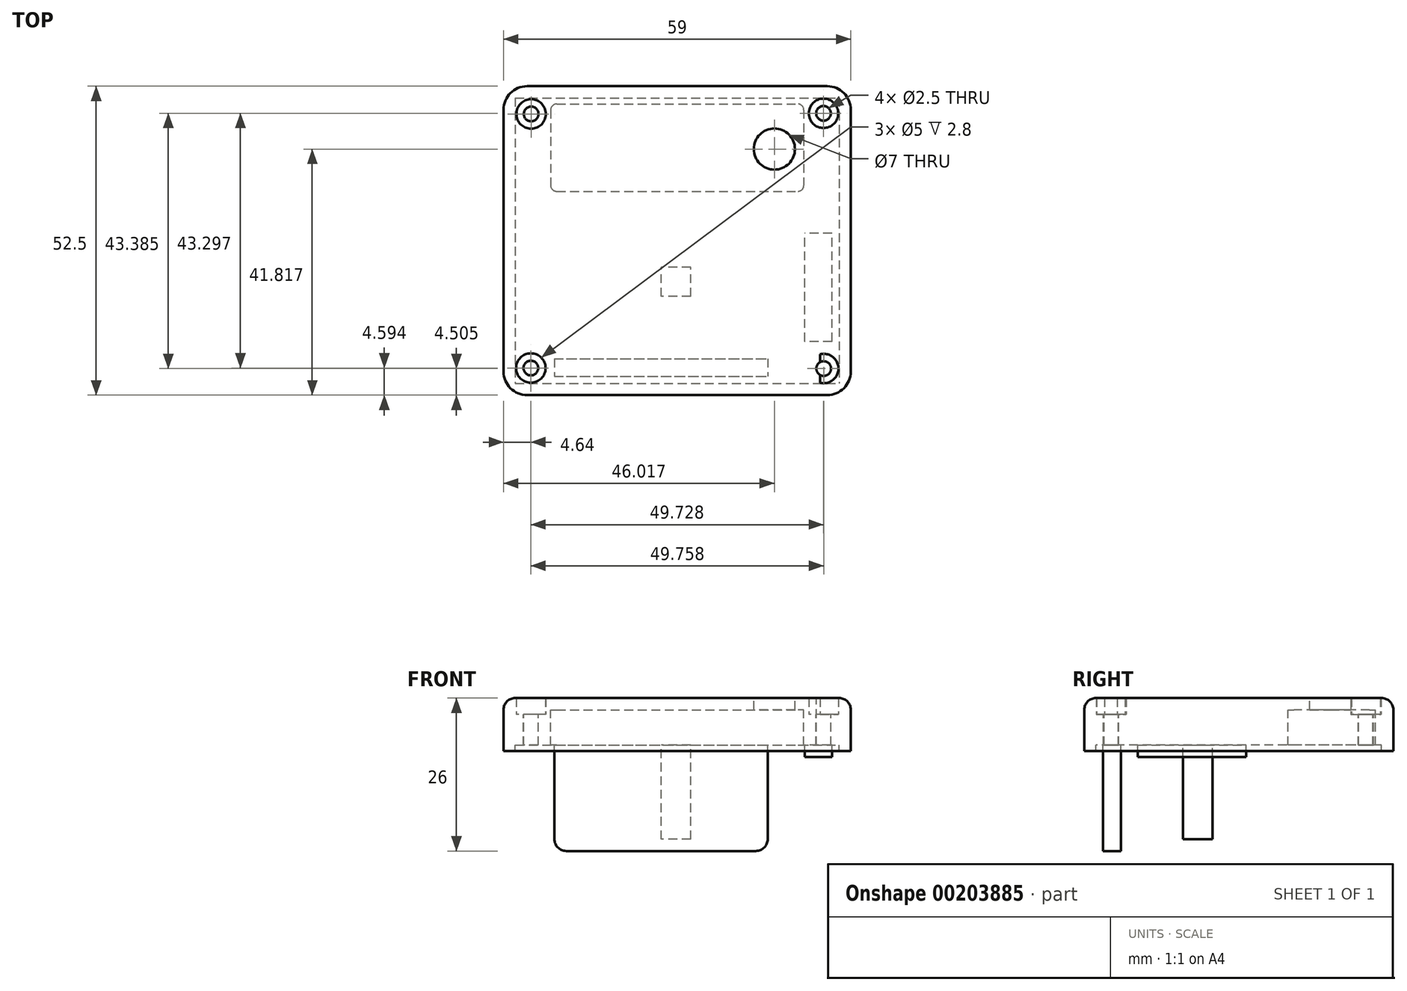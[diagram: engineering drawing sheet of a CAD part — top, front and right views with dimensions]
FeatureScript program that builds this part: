
annotation { "Feature Type Name" : "Feature", "Feature Type Description" : "" }
export const myFeature = defineFeature(function(context is Context, id is Id, definition is map)
    precondition{}
    {
        {
            var Q0;
            Q0=qCreatedBy(makeId("Top.planeOp"),FACE);
            var sketch = newSketch(context, id + "F0", { "sketchPlane" : qUnion([Q0])});
            skLineSegment(sketch, "E0.bottom", {"start": v(-36.58, 35.75) * mm, "end": v(22.42, 35.75) * mm});
            skLineSegment(sketch, "E0.top", {"start": v(-36.58, -16.75) * mm, "end": v(22.42, -16.75) * mm});
            skLineSegment(sketch, "E0.left", {"start": v(-36.58, 35.75) * mm, "end": v(-36.58, -16.75) * mm});
            skLineSegment(sketch, "E0.right", {"start": v(22.42, 35.75) * mm, "end": v(22.42, -16.75) * mm});
            skLineSegment(sketch, "E1.bottom", {"start": v(-34.58, 33.75) * mm, "end": v(20.42, 33.75) * mm});
            skLineSegment(sketch, "E1.top", {"start": v(-34.58, -14.75) * mm, "end": v(20.42, -14.75) * mm});
            skLineSegment(sketch, "E1.left", {"start": v(-34.58, 33.75) * mm, "end": v(-34.58, -14.75) * mm});
            skLineSegment(sketch, "E1.right", {"start": v(20.42, 33.75) * mm, "end": v(20.42, -14.75) * mm});
            skLineSegment(sketch, "E2.right", {"start": v(-34.58, -2) * mm, "end": v(-34.58, 2) * mm});
            skLineSegment(sketch, "E3.bottom", {"start": v(-34.58, 33.75) * mm, "end": v(9.72, 33.75) * mm});
            skLineSegment(sketch, "E4.top", {"start": v(-34.58, -14.75) * mm, "end": v(-32.58, -14.75) * mm});
            skLineSegment(sketch, "E4.left", {"start": v(-34.58, -8.75) * mm, "end": v(-34.58, -14.75) * mm});
            skLineSegment(sketch, "E5.bottom", {"start": v(13.36, 33.75) * mm, "end": v(14.86, 33.75) * mm});
            skLineSegment(sketch, "E6.top", {"start": v(16.3, -14.75) * mm, "end": v(14.92, -14.75) * mm});
            skLineSegment(sketch, "E7.bottom", {"start": v(17.21, 9.77) * mm, "end": v(11.21, 9.77) * mm});
            skLineSegment(sketch, "E7.top", {"start": v(17.21, 4.77) * mm, "end": v(11.21, 4.77) * mm});
            skLineSegment(sketch, "E7.left", {"start": v(17.21, 9.77) * mm, "end": v(17.21, 4.77) * mm});
            skLineSegment(sketch, "E7.right", {"start": v(11.21, 9.77) * mm, "end": v(11.21, 4.77) * mm});
            skCircle(sketch, "E8", {"center": v(-31.94, -12.16) * mm, "radius": 1.25 * mm});
            skCircle(sketch, "E9", {"center": v(-31.9, 31.03) * mm, "radius": 2.5 * mm});
            skCircle(sketch, "E10", {"center": v(-31.9, 31.03) * mm, "radius": 1.25 * mm});
            skLineSegment(sketch, "E11", {"start": v(-29.4, 31.03) * mm, "end": v(-29.4, 33.75) * mm});
            skLineSegment(sketch, "E12", {"start": v(-31.9, 28.53) * mm, "end": v(-34.58, 28.53) * mm});
            skLineSegment(sketch, "E13.bottom", {"start": v(17.22, 16.75) * mm, "end": v(-34.58, 16.75) * mm});
            skLineSegment(sketch, "E13.top", {"start": v(17.22, 15.25) * mm, "end": v(-34.58, 15.25) * mm});
            skLineSegment(sketch, "E13.left", {"start": v(17.22, 15.25) * mm, "end": v(17.22, 16.75) * mm});
            skLineSegment(sketch, "E13.right", {"start": v(-34.58, 15.25) * mm, "end": v(-34.58, 16.75) * mm});
            skLineSegment(sketch, "E14.bottom", {"start": v(-34.58, 14.63) * mm, "end": v(-32.58, 14.63) * mm});
            skLineSegment(sketch, "E14.top", {"start": v(-34.58, 8.63) * mm, "end": v(-32.58, 8.63) * mm});
            skLineSegment(sketch, "E14.left", {"start": v(-34.58, 14.63) * mm, "end": v(-34.58, 8.63) * mm});
            skLineSegment(sketch, "E14.right", {"start": v(-32.58, 14.63) * mm, "end": v(-32.58, 8.63) * mm});
            skCircle(sketch, "E15", {"center": v(17.79, 31.14) * mm, "radius": 2.5 * mm});
            skCircle(sketch, "E16", {"center": v(17.79, 31.14) * mm, "radius": 1.25 * mm});
            skLineSegment(sketch, "E17", {"start": v(17.79, 28.64) * mm, "end": v(20.42, 28.64) * mm});
            skCircle(sketch, "E18", {"center": v(17.82, -12.24) * mm, "radius": 2.5 * mm});
            skCircle(sketch, "E19", {"center": v(17.82, -12.24) * mm, "radius": 1.25 * mm});
            skLineSegment(sketch, "E20", {"start": v(17.82, -9.74) * mm, "end": v(20.42, -9.74) * mm});
            skLineSegment(sketch, "E21.bottom", {"start": v(14.92, -14.75) * mm, "end": v(13.15, -14.75) * mm});
            skLineSegment(sketch, "E21.top", {"start": v(14.92, -13.29) * mm, "end": v(13.15, -13.29) * mm});
            skLineSegment(sketch, "E21.left", {"start": v(14.92, -14.75) * mm, "end": v(14.92, -13.29) * mm});
            skLineSegment(sketch, "E21.right", {"start": v(13.15, -14.75) * mm, "end": v(13.15, -13.29) * mm});
            skLineSegment(sketch, "E22", {"start": v(17.22, 33.75) * mm, "end": v(17.22, -14.75) * mm});
            skLineSegment(sketch, "E23", {"start": v(20.42, -9.02) * mm, "end": v(17.22, -9.02) * mm});
            skLineSegment(sketch, "E24.top", {"start": v(14.92, -7.79) * mm, "end": v(13.15, -7.79) * mm});
            skLineSegment(sketch, "E24.left", {"start": v(14.92, -13.29) * mm, "end": v(14.92, -7.79) * mm});
            skLineSegment(sketch, "E24.right", {"start": v(13.15, -13.29) * mm, "end": v(13.15, -7.79) * mm});
            skLineSegment(sketch, "E25", {"start": v(15.29, 31.14) * mm, "end": v(15.29, 33.75) * mm});
            skLineSegment(sketch, "E26", {"start": v(15.32, -12.24) * mm, "end": v(15.32, -14.75) * mm});
            skLineSegment(sketch, "E27.bottom", {"start": v(-29.94, 15.25) * mm, "end": v(10.06, 15.25) * mm});
            skLineSegment(sketch, "E27.top", {"start": v(-29.94, 13.25) * mm, "end": v(10.06, 13.25) * mm});
            skLineSegment(sketch, "E27.left", {"start": v(-29.94, 15.25) * mm, "end": v(-29.94, 13.25) * mm});
            skLineSegment(sketch, "E27.right", {"start": v(10.06, 15.25) * mm, "end": v(10.06, 13.25) * mm});
            skLineSegment(sketch, "E28.bottom", {"start": v(-19.58, -1.75) * mm, "end": v(5.42, -1.75) * mm});
            skLineSegment(sketch, "E28.top", {"start": v(-19.58, 7.25) * mm, "end": v(5.42, 7.25) * mm});
            skLineSegment(sketch, "E28.left", {"start": v(-19.58, -1.75) * mm, "end": v(-19.58, 7.25) * mm});
            skLineSegment(sketch, "E28.right", {"start": v(5.42, -1.75) * mm, "end": v(5.42, 7.25) * mm});
            skCircle(sketch, "E29", {"center": v(9.44, 25.07) * mm, "radius": 3.5 * mm});
            skLineSegment(sketch, "E30", {"start": v(-29.58, 15.25) * mm, "end": v(-29.58, -14.75) * mm, "construction": true});
            skLineSegment(sketch, "E31", {"start": v(17.22, 1.25) * mm, "end": v(-34.58, 1.25) * mm, "construction": true});
            skLineSegment(sketch, "E32", {"start": v(-34.58, 6.25) * mm, "end": v(17.21, 6.25) * mm, "construction": true});
            skLineSegment(sketch, "E33.bottom", {"start": v(-27.94, -10.55) * mm, "end": v(8.3, -10.55) * mm});
            skLineSegment(sketch, "E33.top", {"start": v(-27.94, -13.55) * mm, "end": v(8.3, -13.55) * mm});
            skLineSegment(sketch, "E33.left", {"start": v(-27.94, -10.55) * mm, "end": v(-27.94, -13.55) * mm});
            skLineSegment(sketch, "E33.right", {"start": v(8.3, -10.55) * mm, "end": v(8.3, -13.55) * mm});
            skCircle(sketch, "E34", {"center": v(-31.94, -12.16) * mm, "radius": 2.5 * mm});
            skLineSegment(sketch, "E35.bottom", {"start": v(-28.56, 32.72) * mm, "end": v(14.44, 32.72) * mm});
            skLineSegment(sketch, "E35.top", {"start": v(-28.56, 17.89) * mm, "end": v(14.44, 17.89) * mm});
            skLineSegment(sketch, "E35.left", {"start": v(-28.56, 32.72) * mm, "end": v(-28.56, 17.89) * mm});
            skLineSegment(sketch, "E35.right", {"start": v(14.44, 32.72) * mm, "end": v(14.44, 17.89) * mm});
            skLineSegment(sketch, "E36.bottom", {"start": v(-4.78, 0) * mm, "end": v(-9.78, 0) * mm});
            skLineSegment(sketch, "E36.top", {"start": v(-4.78, 5) * mm, "end": v(-9.78, 5) * mm});
            skLineSegment(sketch, "E36.left", {"start": v(-4.78, 0) * mm, "end": v(-4.78, 5) * mm});
            skLineSegment(sketch, "E36.right", {"start": v(-9.78, 0) * mm, "end": v(-9.78, 5) * mm});
            skSolve(sketch);
        }
        {
            var Q0;
            Q0=qCreatedBy(makeId("Top.planeOp"),FACE);
            var sketch = newSketch(context, id + "F1", { "sketchPlane" : qUnion([Q0])});
            skLineSegment(sketch, "E37.bottom", {"start": v(-36.58, 35.75) * mm, "end": v(22.42, 35.75) * mm});
            skLineSegment(sketch, "E37.top", {"start": v(-36.58, -16.75) * mm, "end": v(22.42, -16.75) * mm});
            skLineSegment(sketch, "E37.left", {"start": v(-36.58, 35.75) * mm, "end": v(-36.58, -16.75) * mm});
            skLineSegment(sketch, "E37.right", {"start": v(22.42, 35.75) * mm, "end": v(22.42, -16.75) * mm});
            skLineSegment(sketch, "E38.bottom", {"start": v(-34.58, 33.75) * mm, "end": v(20.42, 33.75) * mm});
            skLineSegment(sketch, "E38.top", {"start": v(-34.58, -14.75) * mm, "end": v(20.42, -14.75) * mm});
            skLineSegment(sketch, "E38.left", {"start": v(-34.58, 33.75) * mm, "end": v(-34.58, -14.75) * mm});
            skLineSegment(sketch, "E38.right", {"start": v(20.42, 33.75) * mm, "end": v(20.42, -14.75) * mm});
            skSolve(sketch);
        }
        {
            var Q0;
            Q0=qCreatedBy(makeId("Top.planeOp"),FACE);
            var sketch = newSketch(context, id + "F2", { "sketchPlane" : qUnion([Q0])});
            skLineSegment(sketch, "E39.bottom", {"start": v(-32.68, -7.56) * mm, "end": v(-26.46, -7.56) * mm});
            skLineSegment(sketch, "E39.top", {"start": v(-32.68, 10.68) * mm, "end": v(-26.46, 10.68) * mm});
            skLineSegment(sketch, "E39.left", {"start": v(-32.68, -7.56) * mm, "end": v(-32.68, 10.68) * mm});
            skLineSegment(sketch, "E39.right", {"start": v(-26.46, -7.56) * mm, "end": v(-26.46, 10.68) * mm});
            skSolve(sketch);
        }
        {
            var Q0;
            Q0=makeQuery(id+"F1.imprint","IMPRINT",FACE,{"disambiguationData":[TD([[makeQuery(id+"F1.imprint","IMPRINT",EDGE,{"derivedFrom":sQuery(id+"F1.wireOp",EDGE,"E38.bottom")}),-1.0]])]});
            extrude(context, id + "F3", {"entities" : qUnion([Q0]), "oppositeDirection" : true, "depth" : 8 * mm});
        }
        {
            var Q0;
            Q0=makeQuery(id+"F1.imprint","IMPRINT",FACE,{"disambiguationData":[TD([[makeQuery(id+"F1.imprint","IMPRINT",EDGE,{"derivedFrom":sQuery(id+"F1.wireOp",EDGE,"E37.bottom")}),-1.0]])]});
            extrude(context, id + "F4", {"entities" : qUnion([Q0]), "operationType" : NewBodyOperationType.ADD, "oppositeDirection" : true, "depth" : 9 * mm});
        }
        {
            var Q0;
            {var subQ0=sQuery(id+"F0.wireOp",EDGE,"E8");var subQ1=sQuery(id+"F0.wireOp",EDGE,"E4.right");var subQ2=makeQuery(id+"F0.imprint","INTERSECT",VERTEX,{"disambiguationData":[OD(0.0)],"derivedFrom":[subQ1,subQ0]});Q0=makeQuery(id+"F0.imprint","IMPRINT",FACE,{"disambiguationData":[TD([[makeQuery(id+"F0.imprint","IMPRINT",EDGE,{"disambiguationData":[TD([[subQ2,-1.0]])],"derivedFrom":subQ1}),1.0]])]});}
            var Q1;
            {var subQ0=sQuery(id+"F0.wireOp",EDGE,"E8");var subQ1=sQuery(id+"F0.wireOp",EDGE,"E4.right");var subQ2=makeQuery(id+"F0.imprint","INTERSECT",VERTEX,{"disambiguationData":[OD(0.0)],"derivedFrom":[subQ1,subQ0]});Q1=makeQuery(id+"F0.imprint","IMPRINT",FACE,{"disambiguationData":[TD([[makeQuery(id+"F0.imprint","IMPRINT",EDGE,{"disambiguationData":[TD([[subQ2,-1.0]])],"derivedFrom":subQ1}),-1.0]])]});}
            var Q2;
            Q2=makeQuery(id+"F0.imprint","IMPRINT",FACE,{"disambiguationData":[TD([[makeQuery(id+"F0.imprint","IMPRINT",EDGE,{"derivedFrom":sQuery(id+"F0.wireOp",EDGE,"E10")}),1.0]])]});
            var Q3;
            {var subQ0=sQuery(id+"F0.wireOp",EDGE,"E22");var subQ1=sQuery(id+"F0.wireOp",EDGE,"E19");var subQ2=makeQuery(id+"F0.imprint","INTERSECT",VERTEX,{"disambiguationData":[OD(0.0)],"derivedFrom":[subQ1,subQ0]});Q3=makeQuery(id+"F0.imprint","IMPRINT",FACE,{"disambiguationData":[TD([[makeQuery(id+"F0.imprint","IMPRINT",EDGE,{"disambiguationData":[TD([[subQ2,1.0]])],"derivedFrom":subQ1}),1.0]])]});}
            var Q4;
            {var subQ0=sQuery(id+"F0.wireOp",EDGE,"E22");var subQ1=sQuery(id+"F0.wireOp",EDGE,"E19");var subQ2=makeQuery(id+"F0.imprint","INTERSECT",VERTEX,{"disambiguationData":[OD(0.0)],"derivedFrom":[subQ1,subQ0]});Q4=makeQuery(id+"F0.imprint","IMPRINT",FACE,{"disambiguationData":[TD([[makeQuery(id+"F0.imprint","IMPRINT",EDGE,{"disambiguationData":[TD([[subQ2,-1.0]])],"derivedFrom":subQ1}),1.0]])]});}
            var Q5;
            Q5=makeQuery(id+"F0.imprint","IMPRINT",FACE,{"disambiguationData":[TD([[makeQuery(id+"F0.imprint","IMPRINT",EDGE,{"derivedFrom":sQuery(id+"F0.wireOp",EDGE,"E29")}),1.0]])]});
            var Q6;
            {var subQ0=sQuery(id+"F0.wireOp",EDGE,"E22");var subQ1=sQuery(id+"F0.wireOp",EDGE,"E16");var subQ2=makeQuery(id+"F0.imprint","INTERSECT",VERTEX,{"disambiguationData":[OD(0.0)],"derivedFrom":[subQ1,subQ0]});Q6=makeQuery(id+"F0.imprint","IMPRINT",FACE,{"disambiguationData":[TD([[makeQuery(id+"F0.imprint","IMPRINT",EDGE,{"disambiguationData":[TD([[subQ2,1.0]])],"derivedFrom":subQ1}),1.0]])]});}
            var Q7;
            {var subQ0=sQuery(id+"F0.wireOp",EDGE,"E22");var subQ1=sQuery(id+"F0.wireOp",EDGE,"E16");var subQ2=makeQuery(id+"F0.imprint","INTERSECT",VERTEX,{"disambiguationData":[OD(0.0)],"derivedFrom":[subQ1,subQ0]});Q7=makeQuery(id+"F0.imprint","IMPRINT",FACE,{"disambiguationData":[TD([[makeQuery(id+"F0.imprint","IMPRINT",EDGE,{"disambiguationData":[TD([[subQ2,-1.0]])],"derivedFrom":subQ1}),1.0]])]});}
            var Q8;
            Q8=makeQuery(id+"F0.imprint","IMPRINT",FACE,{"disambiguationData":[TD([[makeQuery(id+"F0.imprint","IMPRINT",EDGE,{"derivedFrom":sQuery(id+"F0.wireOp",EDGE,"E8")}),1.0]])]});
            extrude(context, id + "F5", {"entities" : qUnion([Q0, Q1, Q2, Q3, Q4, Q5, Q6, Q7, Q8]), "operationType" : NewBodyOperationType.REMOVE, "oppositeDirection" : true, "depth" : 9.6 * mm});
        }
        {
            var Q0;
            Q0=makeQuery(id+"F2.imprint","IMPRINT",FACE,{"disambiguationData":[TD([[makeQuery(id+"F2.imprint","IMPRINT",EDGE,{"derivedFrom":sQuery(id+"F2.wireOp",EDGE,"E39.bottom")}),1.0]])]});
            extrude(context, id + "F6", {"entities" : qUnion([Q0]), "operationType" : NewBodyOperationType.ADD, "oppositeDirection" : true, "depth" : 4.07 * mm});
        }
        {
            var Q0;
            Q0=makeQuery(id+"F0.imprint","IMPRINT",FACE,{"disambiguationData":[TD([[makeQuery(id+"F0.imprint","IMPRINT",EDGE,{"derivedFrom":sQuery(id+"F0.wireOp",EDGE,"E33.bottom")}),-1.0]])]});
            var Q1;
            Q1=makeQuery(id+"F0.imprint","IMPRINT",FACE,{"disambiguationData":[TD([[makeQuery(id+"F0.imprint","IMPRINT",EDGE,{"derivedFrom":sQuery(id+"F0.wireOp",EDGE,"E27.bottom")}),-1.0]])]});
            extrude(context, id + "F7", {"entities" : qUnion([Q0, Q1]), "operationType" : NewBodyOperationType.ADD, "oppositeDirection" : true, "depth" : 26 * mm});
        }
        {
            var Q0;
            Q0=makeQuery(id+"F7.opExtrude","CAP_EDGE",EDGE,{"disambiguationData":[OSD([sQuery(id+"F0.wireOp",EDGE,"E33.right")])],"isStart":false});
            var Q1;
            Q1=makeQuery(id+"F7.opExtrude","CAP_EDGE",EDGE,{"disambiguationData":[OSD([sQuery(id+"F0.wireOp",EDGE,"E33.left")])],"isStart":false});
            var Q2;
            Q2=makeQuery(id+"F7.opExtrude","CAP_EDGE",EDGE,{"disambiguationData":[OSD([sQuery(id+"F0.wireOp",EDGE,"E27.left")])],"isStart":false});
            var Q3;
            Q3=makeQuery(id+"F7.opExtrude","CAP_EDGE",EDGE,{"disambiguationData":[OSD([sQuery(id+"F0.wireOp",EDGE,"E27.right")])],"isStart":false});
            fillet(context, id + "F8", {"entities" : qUnion([Q0, Q1, Q2, Q3]), "radius" : 2 * mm, "tangentPropagation" : true, "allowEdgeOverflow" : false});
        }
        {
            var Q0;
            Q0=makeQuery(id+"F4.opExtrude","SWEPT_EDGE",EDGE,{"disambiguationData":[OSD([sQuery(id+"F1.wireOp",EDGE,"E37.top"),sQuery(id+"F1.wireOp",EDGE,"E37.right")])]});
            var Q1;
            Q1=makeQuery(id+"F4.opExtrude","SWEPT_EDGE",EDGE,{"disambiguationData":[OSD([sQuery(id+"F1.wireOp",EDGE,"E37.bottom"),sQuery(id+"F1.wireOp",EDGE,"E37.right")])]});
            var Q2;
            Q2=makeQuery(id+"F4.opExtrude","SWEPT_EDGE",EDGE,{"disambiguationData":[OSD([sQuery(id+"F1.wireOp",EDGE,"E37.top"),sQuery(id+"F1.wireOp",EDGE,"E37.left")])]});
            var Q3;
            Q3=makeQuery(id+"F4.opExtrude","SWEPT_EDGE",EDGE,{"disambiguationData":[OSD([sQuery(id+"F1.wireOp",EDGE,"E37.bottom"),sQuery(id+"F1.wireOp",EDGE,"E37.left")])]});
            fillet(context, id + "F9", {"entities" : qUnion([Q0, Q1, Q2, Q3]), "radius" : 4 * mm, "tangentPropagation" : true, "allowEdgeOverflow" : false});
        }
        {
            var Q0;
            Q0=qCreatedBy(makeId("Top.planeOp"),FACE);
            var sketch = newSketch(context, id + "F10", { "sketchPlane" : qUnion([Q0])});
            skLineSegment(sketch, "E40.bottom", {"start": v(19.24, -7.64) * mm, "end": v(14.64, -7.64) * mm});
            skLineSegment(sketch, "E40.top", {"start": v(19.24, 10.77) * mm, "end": v(14.64, 10.77) * mm});
            skLineSegment(sketch, "E40.left", {"start": v(19.24, -7.64) * mm, "end": v(19.24, 10.77) * mm});
            skLineSegment(sketch, "E40.right", {"start": v(14.64, -7.64) * mm, "end": v(14.64, 10.77) * mm});
            skSolve(sketch);
        }
        {
            var Q0;
            Q0=qSketchRegion(id+"F10",true);
            extrude(context, id + "F11", {"entities" : qUnion([Q0]), "operationType" : NewBodyOperationType.ADD, "oppositeDirection" : true, "depth" : 10 * mm});
        }
        {
            var Q0;
            Q0=makeQuery(id+"F0.imprint","IMPRINT",FACE,{"disambiguationData":[TD([[makeQuery(id+"F0.imprint","IMPRINT",EDGE,{"derivedFrom":sQuery(id+"F0.wireOp",EDGE,"E29")}),-1.0]])]});
            extrude(context, id + "F12", {"entities" : qUnion([Q0]), "operationType" : NewBodyOperationType.REMOVE, "oppositeDirection" : true, "depth" : 25 * mm, "hasSecondDirection" : true, "secondDirectionOppositeDirection" : true, "secondDirectionDepth" : 2 * mm});
        }
        {
            var Q0;
            {var subQ4=sQuery(id+"F0.wireOp",EDGE,"E18");var subQ5=makeQuery(id+"F0.imprint","INTERSECT",VERTEX,{"derivedFrom":[subQ4,sQuery(id+"F0.wireOp",EDGE,"E26")]});Q0=makeQuery(id+"F0.imprint","IMPRINT",FACE,{"disambiguationData":[TD([[makeQuery(id+"F0.imprint","IMPRINT",EDGE,{"disambiguationData":[TD([[subQ5,1.0]])],"derivedFrom":subQ4}),1.0]])]});}
            var Q1;
            {var subQ1=sQuery(id+"F0.wireOp",EDGE,"E18");var subQ6=makeQuery(id+"F0.imprint","INTERSECT",VERTEX,{"derivedFrom":[subQ1,sQuery(id+"F0.wireOp",EDGE,"E20")]});Q1=makeQuery(id+"F0.imprint","IMPRINT",FACE,{"disambiguationData":[TD([[makeQuery(id+"F0.imprint","IMPRINT",EDGE,{"disambiguationData":[TD([[subQ6,-1.0]])],"derivedFrom":subQ1}),1.0]])]});}
            var Q2;
            Q2=makeQuery(id+"F0.imprint","IMPRINT",FACE,{"disambiguationData":[TD([[makeQuery(id+"F0.imprint","IMPRINT",EDGE,{"derivedFrom":sQuery(id+"F0.wireOp",EDGE,"E10")}),-1.0]])]});
            var Q3;
            {var subQ0=sQuery(id+"F0.wireOp",EDGE,"PLKqhVFR-8eKu-Ixv1-GPgQ-gXaM0qRD25Is");var subQ2=sQuery(id+"F0.wireOp",EDGE,"E4.right");var subQ7=makeQuery(id+"F0.imprint","INTERSECT",VERTEX,{"disambiguationData":[OD(0.0)],"derivedFrom":[subQ2,subQ0]});Q3=makeQuery(id+"F0.imprint","IMPRINT",FACE,{"disambiguationData":[TD([[makeQuery(id+"F0.imprint","IMPRINT",EDGE,{"disambiguationData":[TD([[subQ7,-1.0]])],"derivedFrom":subQ2}),1.0]])]});}
            var Q4;
            {var subQ0=sQuery(id+"F0.wireOp",EDGE,"PLKqhVFR-8eKu-Ixv1-GPgQ-gXaM0qRD25Is");var subQ1=sQuery(id+"F0.wireOp",EDGE,"E4.right");var subQ2=makeQuery(id+"F0.imprint","INTERSECT",VERTEX,{"disambiguationData":[OD(0.0)],"derivedFrom":[subQ1,subQ0]});Q4=makeQuery(id+"F0.imprint","IMPRINT",FACE,{"disambiguationData":[TD([[makeQuery(id+"F0.imprint","IMPRINT",EDGE,{"disambiguationData":[TD([[subQ2,-1.0]])],"derivedFrom":subQ1}),-1.0]])]});}
            var Q5;
            {var subQ1=sQuery(id+"F0.wireOp",EDGE,"E15");var subQ6=makeQuery(id+"F0.imprint","INTERSECT",VERTEX,{"derivedFrom":[subQ1,sQuery(id+"F0.wireOp",EDGE,"E25")]});Q5=makeQuery(id+"F0.imprint","IMPRINT",FACE,{"disambiguationData":[TD([[makeQuery(id+"F0.imprint","IMPRINT",EDGE,{"disambiguationData":[TD([[subQ6,1.0]])],"derivedFrom":subQ1}),1.0]])]});}
            var Q6;
            {var subQ4=sQuery(id+"F0.wireOp",EDGE,"E15");var subQ6=makeQuery(id+"F0.imprint","INTERSECT",VERTEX,{"derivedFrom":[subQ4,sQuery(id+"F0.wireOp",EDGE,"E17")]});Q6=makeQuery(id+"F0.imprint","IMPRINT",FACE,{"disambiguationData":[TD([[makeQuery(id+"F0.imprint","IMPRINT",EDGE,{"disambiguationData":[TD([[subQ6,1.0]])],"derivedFrom":subQ4}),1.0]])]});}
            var Q7;
            {var subQ3=sQuery(id+"F0.wireOp",EDGE,"E34");var subQ5=sQuery(id+"F0.wireOp",EDGE,"E4.right");var subQ6=makeQuery(id+"F0.imprint","INTERSECT",VERTEX,{"disambiguationData":[OD(0.0)],"derivedFrom":[subQ5,subQ3]});Q7=makeQuery(id+"F0.imprint","IMPRINT",FACE,{"disambiguationData":[TD([[makeQuery(id+"F0.imprint","IMPRINT",EDGE,{"disambiguationData":[TD([[subQ6,-1.0]])],"derivedFrom":subQ5}),1.0]])]});}
            var Q8;
            {var subQ1=sQuery(id+"F0.wireOp",EDGE,"E4.right");var subQ6=sQuery(id+"F0.wireOp",EDGE,"kjhwjDdY-w9so-hjMB-xEs9-QlES4Zc8QczL");var subQ7=makeQuery(id+"F0.imprint","INTERSECT",VERTEX,{"derivedFrom":[subQ1,subQ6]});Q8=makeQuery(id+"F0.imprint","IMPRINT",FACE,{"disambiguationData":[TD([[makeQuery(id+"F0.imprint","IMPRINT",EDGE,{"disambiguationData":[TD([[subQ7,-1.0]])],"derivedFrom":subQ1}),-1.0]])]});}
            var Q9;
            {var subQ0=sQuery(id+"F0.wireOp",EDGE,"E34");var subQ1=sQuery(id+"F0.wireOp",EDGE,"E4.right");var subQ2=makeQuery(id+"F0.imprint","INTERSECT",VERTEX,{"disambiguationData":[OD(0.0)],"derivedFrom":[subQ1,subQ0]});Q9=makeQuery(id+"F0.imprint","IMPRINT",FACE,{"disambiguationData":[TD([[makeQuery(id+"F0.imprint","IMPRINT",EDGE,{"disambiguationData":[TD([[subQ2,-1.0]])],"derivedFrom":subQ1}),-1.0]])]});}
            var Q10;
            Q10=makeQuery(id+"F0.imprint","IMPRINT",FACE,{"disambiguationData":[TD([[makeQuery(id+"F0.imprint","IMPRINT",EDGE,{"derivedFrom":sQuery(id+"F0.wireOp",EDGE,"E8")}),-1.0]])]});
            extrude(context, id + "F13", {"entities" : qUnion([Q0, Q1, Q2, Q3, Q4, Q5, Q6, Q7, Q8, Q9, Q10]), "operationType" : NewBodyOperationType.REMOVE, "depth" : 3.9 * mm, "hasSecondDirection" : true, "secondDirectionOppositeDirection" : true, "secondDirectionDepth" : 2.8 * mm});
        }
        {
            var Q0;
            Q0=makeQuery(id+"F0.imprint","IMPRINT",FACE,{"disambiguationData":[TD([[makeQuery(id+"F0.imprint","IMPRINT",EDGE,{"derivedFrom":sQuery(id+"F0.wireOp",EDGE,"EeBKnc5o-wB0O-0N6T-5B69-5pySvWSWUYzF")}),-1.0]])]});
            var Q1;
            Q1=makeQuery(id+"F0.imprint","IMPRINT",FACE,{"disambiguationData":[TD([[makeQuery(id+"F0.imprint","IMPRINT",EDGE,{"derivedFrom":sQuery(id+"F0.wireOp",EDGE,"E29")}),-1.0]])]});
            extrude(context, id + "F14", {"entities" : qUnion([Q0, Q1]), "operationType" : NewBodyOperationType.REMOVE, "oppositeDirection" : true, "depth" : 15 * mm, "hasSecondDirection" : true, "secondDirectionOppositeDirection" : true, "secondDirectionDepth" : 2 * mm});
        }
        {
            var Q0;
            Q0=makeQuery(id+"F12.boolean.opBoolean","COPY",EDGE,{"derivedFrom":makeQuery(id+"F12.opExtrude","SWEPT_EDGE",EDGE,{"disambiguationData":[OSD([sQuery(id+"F0.wireOp",EDGE,"E35.bottom"),sQuery(id+"F0.wireOp",EDGE,"E35.left")])]})});
            var Q1;
            Q1=makeQuery(id+"F12.boolean.opBoolean","COPY",EDGE,{"derivedFrom":makeQuery(id+"F12.opExtrude","SWEPT_EDGE",EDGE,{"disambiguationData":[OSD([sQuery(id+"F0.wireOp",EDGE,"E35.top"),sQuery(id+"F0.wireOp",EDGE,"E35.left")])]})});
            var Q2;
            Q2=makeQuery(id+"F12.boolean.opBoolean","COPY",EDGE,{"derivedFrom":makeQuery(id+"F12.opExtrude","SWEPT_EDGE",EDGE,{"disambiguationData":[OSD([sQuery(id+"F0.wireOp",EDGE,"E35.top"),sQuery(id+"F0.wireOp",EDGE,"E35.right")])]})});
            var Q3;
            Q3=makeQuery(id+"F12.boolean.opBoolean","COPY",EDGE,{"derivedFrom":makeQuery(id+"F12.opExtrude","SWEPT_EDGE",EDGE,{"disambiguationData":[OSD([sQuery(id+"F0.wireOp",EDGE,"E35.bottom"),sQuery(id+"F0.wireOp",EDGE,"E35.right")])]})});
            fillet(context, id + "F15", {"entities" : qUnion([Q0, Q1, Q2, Q3]), "radius" : 1 * mm, "tangentPropagation" : true, "allowEdgeOverflow" : false});
        }
        {
            var Q0;
            Q0=makeQuery(id+"F4.opExtrude","CAP_EDGE",EDGE,{"disambiguationData":[OSD([sQuery(id+"F1.wireOp",EDGE,"E37.bottom")])],"isStart":true});
            fillet(context, id + "F16", {"entities" : qUnion([Q0]), "radius" : 2 * mm, "tangentPropagation" : true, "allowEdgeOverflow" : false});
        }
        {
            var Q0;
            Q0=makeQuery(id+"F0.imprint","IMPRINT",FACE,{"disambiguationData":[TD([[makeQuery(id+"F0.imprint","IMPRINT",EDGE,{"derivedFrom":sQuery(id+"F0.wireOp",EDGE,"E36.bottom")}),-1.0]])]});
            extrude(context, id + "F17", {"entities" : qUnion([Q0]), "operationType" : NewBodyOperationType.ADD, "oppositeDirection" : true, "depth" : 24 * mm});
        }
    });
